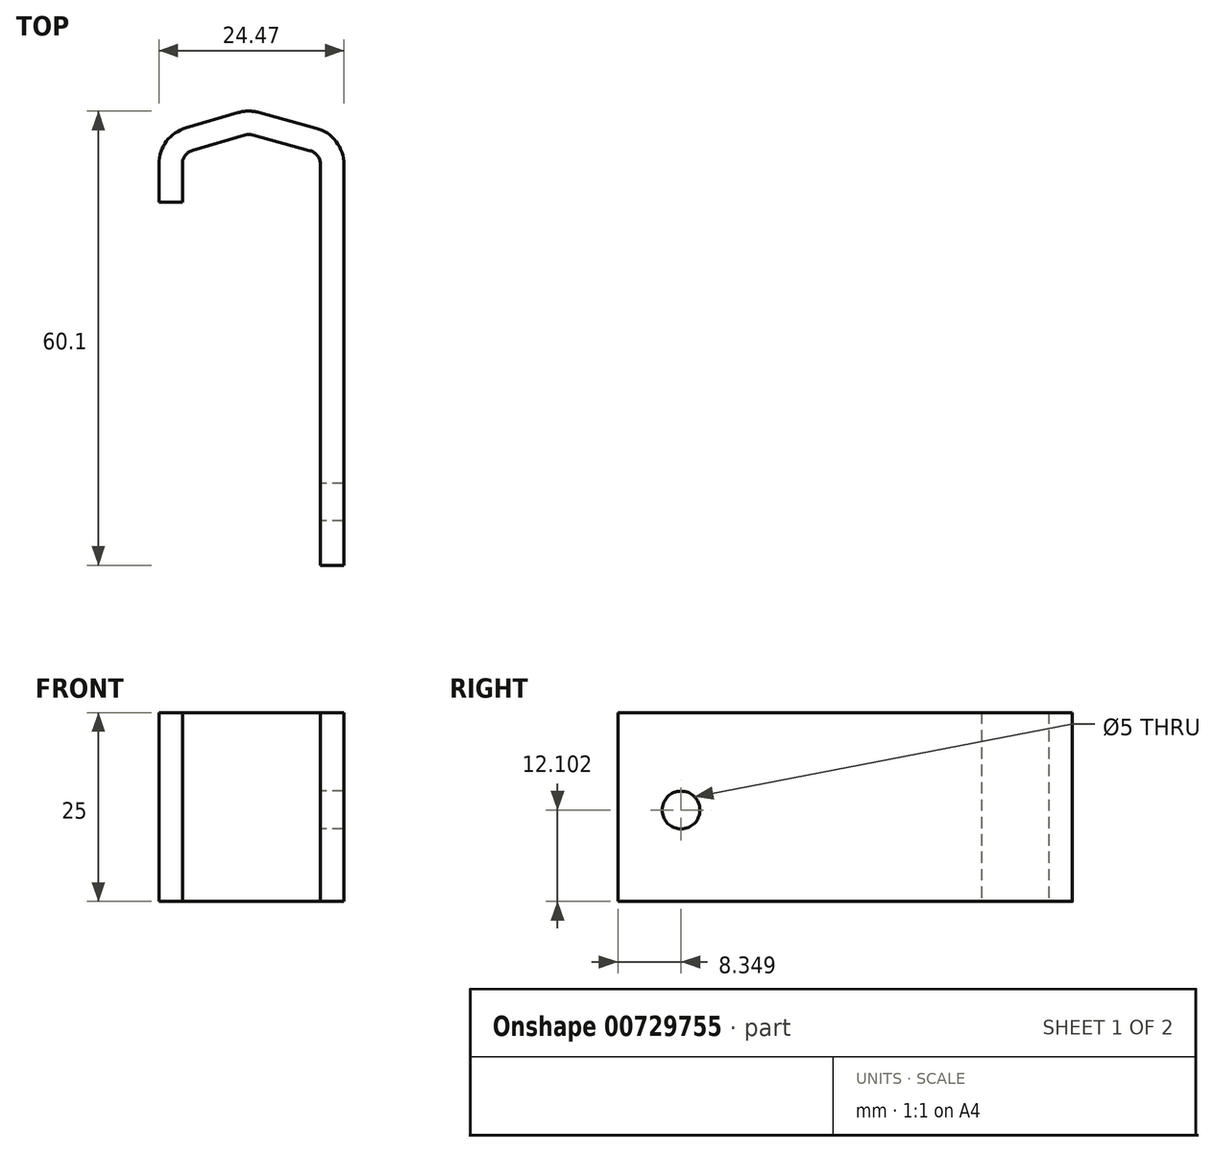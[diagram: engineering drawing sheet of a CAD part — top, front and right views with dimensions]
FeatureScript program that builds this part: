
annotation { "Feature Type Name" : "Feature", "Feature Type Description" : "" }
export const myFeature = defineFeature(function(context is Context, id is Id, definition is map)
    precondition{}
    {
        {
            var Q0;
            Q0=qCreatedBy(makeId("Top.planeOp"),FACE);
            var sketch = newSketch(context, id + "F0", { "sketchPlane" : qUnion([Q0])});
            skLineSegment(sketch, "E0", {"start": v(-11.85, 1.07) * mm, "end": v(-11.85, 6.1) * mm});
            skLineSegment(sketch, "E1", {"start": v(-8.25, 10.9) * mm, "end": v(-1.36, 12.9) * mm});
            skLineSegment(sketch, "E2", {"start": v(1.36, 12.93) * mm, "end": v(8.94, 10.86) * mm});
            skLineSegment(sketch, "E3", {"start": v(12.62, 6.03) * mm, "end": v(12.62, -46.99) * mm});
            skLineSegment(sketch, "E4", {"start": v(-11.85, 9.85) * mm, "end": v(12.62, 9.85) * mm, "construction": true});
            skPoint(sketch, "E5.visualSharp", {"position": v(0, 13.3) * mm});
            skArc(sketch, "E5.filletArc", {"start": v(1.36, 12.93) * mm, "mid": v(0, 13.1) * mm, "end": v(-1.36, 12.9) * mm});
            skPoint(sketch, "E6.visualSharp", {"position": v(12.62, 9.85) * mm});
            skArc(sketch, "E6.filletArc", {"start": v(12.62, 6.03) * mm, "mid": v(11.6, 9.07) * mm, "end": v(8.94, 10.86) * mm});
            skPoint(sketch, "E7.visualSharp", {"position": v(-11.85, 9.85) * mm});
            skArc(sketch, "E7.filletArc", {"start": v(-8.25, 10.9) * mm, "mid": v(-10.85, 9.1) * mm, "end": v(-11.85, 6.1) * mm});
            skLineSegment(sketch, "E8.0", {"start": v(9.52, 6.03) * mm, "end": v(9.52, -46.99) * mm});
            skArc(sketch, "E8.1", {"start": v(9.52, 6.03) * mm, "mid": v(9.13, 7.19) * mm, "end": v(8.12, 7.87) * mm});
            skLineSegment(sketch, "E8.2", {"start": v(0.54, 9.94) * mm, "end": v(8.12, 7.87) * mm});
            skLineSegment(sketch, "E8.3", {"start": v(-8.75, 1.07) * mm, "end": v(-8.75, 6.1) * mm});
            skArc(sketch, "E8.4", {"start": v(-7.38, 7.92) * mm, "mid": v(-8.37, 7.24) * mm, "end": v(-8.75, 6.1) * mm});
            skLineSegment(sketch, "E8.5", {"start": v(-7.38, 7.92) * mm, "end": v(-0.49, 9.93) * mm});
            skArc(sketch, "E8.6", {"start": v(0.54, 9.94) * mm, "mid": v(0.03, 10) * mm, "end": v(-0.49, 9.93) * mm});
            skLineSegment(sketch, "E9", {"start": v(-8.75, 1.07) * mm, "end": v(-11.85, 1.07) * mm});
            skLineSegment(sketch, "E10", {"start": v(9.52, -46.99) * mm, "end": v(12.62, -46.99) * mm});
            skSolve(sketch);
        }
        {
            var Q0;
            Q0=makeQuery(id+"F0.imprint","IMPRINT",FACE,{"disambiguationData":[TD([[makeQuery(id+"F0.imprint","IMPRINT",EDGE,{"derivedFrom":sQuery(id+"F0.wireOp",EDGE,"E0")}),-1.0]])]});
            extrude(context, id + "F1", {"entities" : qUnion([Q0]), "depth" : 25 * mm, "offsetDistance" : 25 * mm});
        }
        {
            var Q0;
            Q0=makeQuery(id+"F1.opExtrude","SWEPT_FACE",FACE,{"disambiguationData":[OSD([sQuery(id+"F0.wireOp",EDGE,"E8.0")])]});
            var sketch = newSketch(context, id + "F2", { "sketchPlane" : qUnion([Q0])});
            skPoint(sketch, "E11", {"position": v(38.64, 12.1) * mm});
            skSolve(sketch);
        }
        {
            var Q0;
            Q0=sQuery(id+"F2.wireOp",VERTEX,"E11");
            var Q1;
            Q1=makeQuery(id+"F1.opExtrude","SWEPT_BODY",BODY,{"disambiguationData":[OSD([sQuery(id+"F0.wireOp",EDGE,"E0"),sQuery(id+"F0.wireOp",EDGE,"E1"),sQuery(id+"F0.wireOp",EDGE,"E2"),sQuery(id+"F0.wireOp",EDGE,"E3"),sQuery(id+"F0.wireOp",EDGE,"E5.filletArc"),sQuery(id+"F0.wireOp",EDGE,"E6.filletArc"),sQuery(id+"F0.wireOp",EDGE,"E7.filletArc"),sQuery(id+"F0.wireOp",EDGE,"E8.0"),sQuery(id+"F0.wireOp",EDGE,"E8.1"),sQuery(id+"F0.wireOp",EDGE,"E8.2"),sQuery(id+"F0.wireOp",EDGE,"E8.3"),sQuery(id+"F0.wireOp",EDGE,"E8.4"),sQuery(id+"F0.wireOp",EDGE,"E8.5"),sQuery(id+"F0.wireOp",EDGE,"E8.6"),sQuery(id+"F0.wireOp",EDGE,"E9"),sQuery(id+"F0.wireOp",EDGE,"E10")])]});
            hole(context, id + "F3", {"style" : HoleStyle.SIMPLE, "endStyle" : HoleEndStyle.THROUGH, "holeDiameter" : 5 * mm, "majorDiameter" : 5 * mm, "isTappedThrough" : true, "tappedDepth" : 12 * mm, "tapClearance" : 3, "locations" : qUnion([Q0]), "scope" : qUnion([Q1])});
        }
    });
